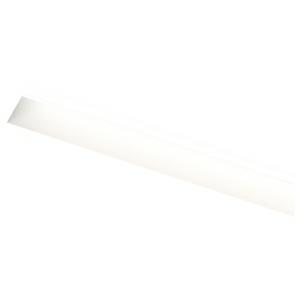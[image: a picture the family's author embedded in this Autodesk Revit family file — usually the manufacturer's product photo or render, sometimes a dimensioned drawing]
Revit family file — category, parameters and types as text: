
# Revit family: groove_l_1440_rl_led_26w_3000k_1704lm_cri80_130-0530_f193
name_source: partatom
category: Leuchten
revit_build: Autodesk Revit 2016 (Build: 20190508_0715(x64)
units: mm (PartAtom-declared; Revit-internal decimal feet)

## family parameters
Basisbauteil = Fläche
Beim Laden mit Abzugskörper schneiden = Nein
Bemaßung runder Anschluss = Durchmesser verwenden
Gemeinsam genutzt = Nein
Lichtquelle = Nein
Raumberechnungspunkt = Nein
Teiletyp = Normal

## types (1)
- 130-0530- (5 x LED, 710 lm, 5.1 W, 3000K)
    Beschreibung = The rimless luminaire GROOVE from the familiy GROOVE consists of aluminum-extruded profile. Charming SOFT-EDGE design ensure unparalleled styling. The ballast is integrated and allows for an operation with 220-240V (50.60Hz). GROOVE (# 130-0530) ist not dimmable (on/off). The luminaire with direct illumination and corresponds to protection class SK1 at IP20.
    CIE Flux Codes = 59 87 97 100 49
    Color Rendering = 1B/80…89
    Color Temperature = 3000K
    Height = 0 mm  [stored 0 ft]
    Hersteller = Prolicht
    Lamp Light Flux = 710 lm
    Lamp Power = 5.1 W
    Lamp count = 5
    Lampe = 5 x LED
    Length = 1440 mm
    Luminous efficacy = 67 lm/W
    ModVariant = Nein
    Modell = 130-0530
    Mounting Place = Ceiling
    Mounting Type = Recessed
    Number of Poles = 1
    OnlyDefault = Ja
    Power Factor = 1
    Product Name = GROOVE L=1440 RL LED 26W 3000K 1704lm CRI80
    Product group = Trimless recessed profile lights
    ProductGroupID = 413
    Protection Class = Protection class
    Protection Degree = Degree of protection
    RLX_Detail_Level = 1
    RlxData = <blob elided: 132777 chars, md5=1de0f398>
    Scheinlast = 26 VA
    Socket = socket
    Standby Power = 0 W
    System Light Flux = 1712 lm
    System Power = 26 W
    Typenbild = 130-0530.jpg
    URL = http://relux.com
    VarID = 130-0530-
    Voltage = 0 V
    Vorgabe-Ansicht = 1800 mm
    Weight = 0.00 kg
    Width = 75 mm

note: [stored X ft] marks values corroborated as IEEE doubles in the binary element streams (Revit-internal decimal feet)

## geometry (parser evidence)
native form markers: Blend x4, Sweep x12
no freeform markers — native parametric forms only
